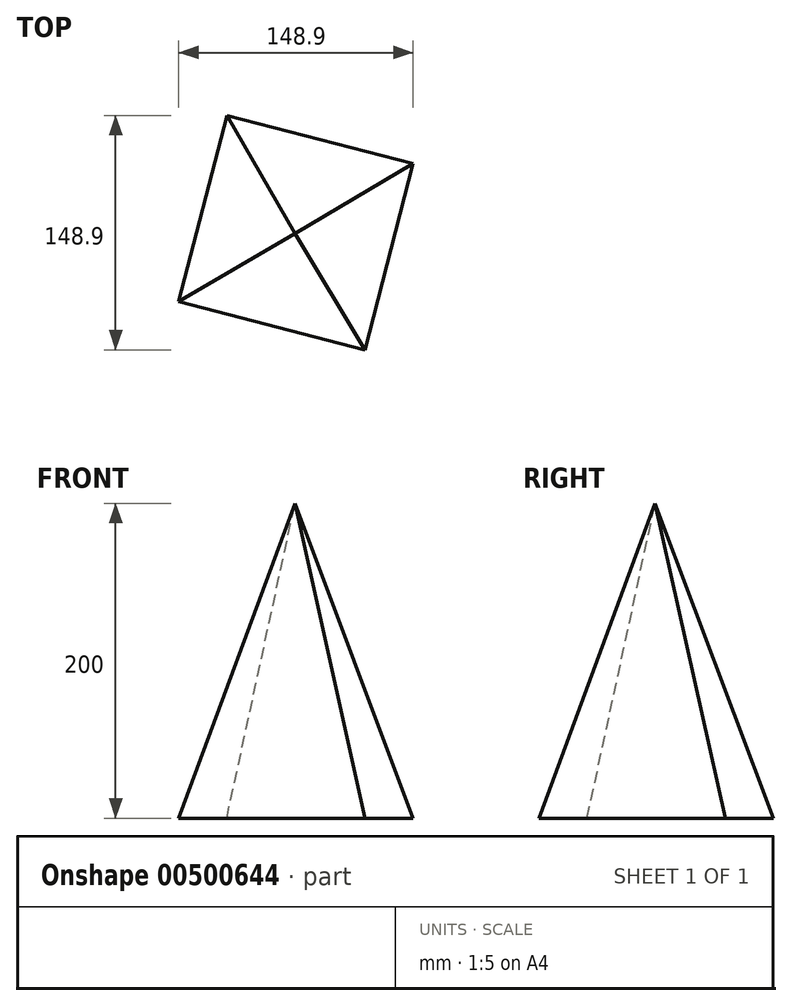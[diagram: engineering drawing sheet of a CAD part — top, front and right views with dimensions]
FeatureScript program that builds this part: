
annotation { "Feature Type Name" : "Feature", "Feature Type Description" : "" }
export const myFeature = defineFeature(function(context is Context, id is Id, definition is map)
    precondition{}
    {
        {
            var Q0;
            Q0=qCreatedBy(makeId("Top.planeOp"),FACE);
            var sketch = newSketch(context, id + "F0", { "sketchPlane" : qUnion([Q0])});
            skCircle(sketch, "E0.cCircle", {"center": v(0, 0) * mm, "radius": 86.42 * mm, "construction": true});
            skLineSegment(sketch, "E0.0", {"start": v(-43.9, 74.45) * mm, "end": v(74.45, 43.9) * mm});
            skLineSegment(sketch, "E0.1", {"start": v(74.45, 43.9) * mm, "end": v(43.9, -74.45) * mm});
            skLineSegment(sketch, "E0.2", {"start": v(43.9, -74.45) * mm, "end": v(-74.45, -43.9) * mm});
            skLineSegment(sketch, "E0.3", {"start": v(-74.45, -43.9) * mm, "end": v(-43.9, 74.45) * mm});
            skSolve(sketch);
        }
        {
            var Q0;
            Q0=qCreatedBy(makeId("Top.planeOp"),FACE);
            cPlane(context, id + "F1", {"entities" : qUnion([Q0]), "cplaneType" : CPlaneType.OFFSET, "offset" : 200 * mm, "width" : 150 * mm, "height" : 150 * mm});
        }
        {
            var Q0;
            Q0=qCreatedBy(id+"F1.planeOp",FACE);
            var sketch = newSketch(context, id + "F2", { "sketchPlane" : qUnion([Q0])});
            skPoint(sketch, "E1", {"position": v(-0.57, -0.72) * mm});
            skSolve(sketch);
        }
        {
            var Q0;
            Q0=makeQuery(id+"F0.imprint","IMPRINT",FACE,{"disambiguationData":[TD([[makeQuery(id+"F0.imprint","IMPRINT",EDGE,{"derivedFrom":sQuery(id+"F0.wireOp",EDGE,"E0.0")}),-1.0]])]});
            var Q1;
            Q1=sQuery(id+"F2.wireOp",VERTEX,"E1");
            loft(context, id + "F3", {"sheetProfilesArray" : [{ "sheetProfileEntities" : qUnion([Q0]) }, { "sheetProfileEntities" : qUnion([Q1]) }]});
        }
    });
